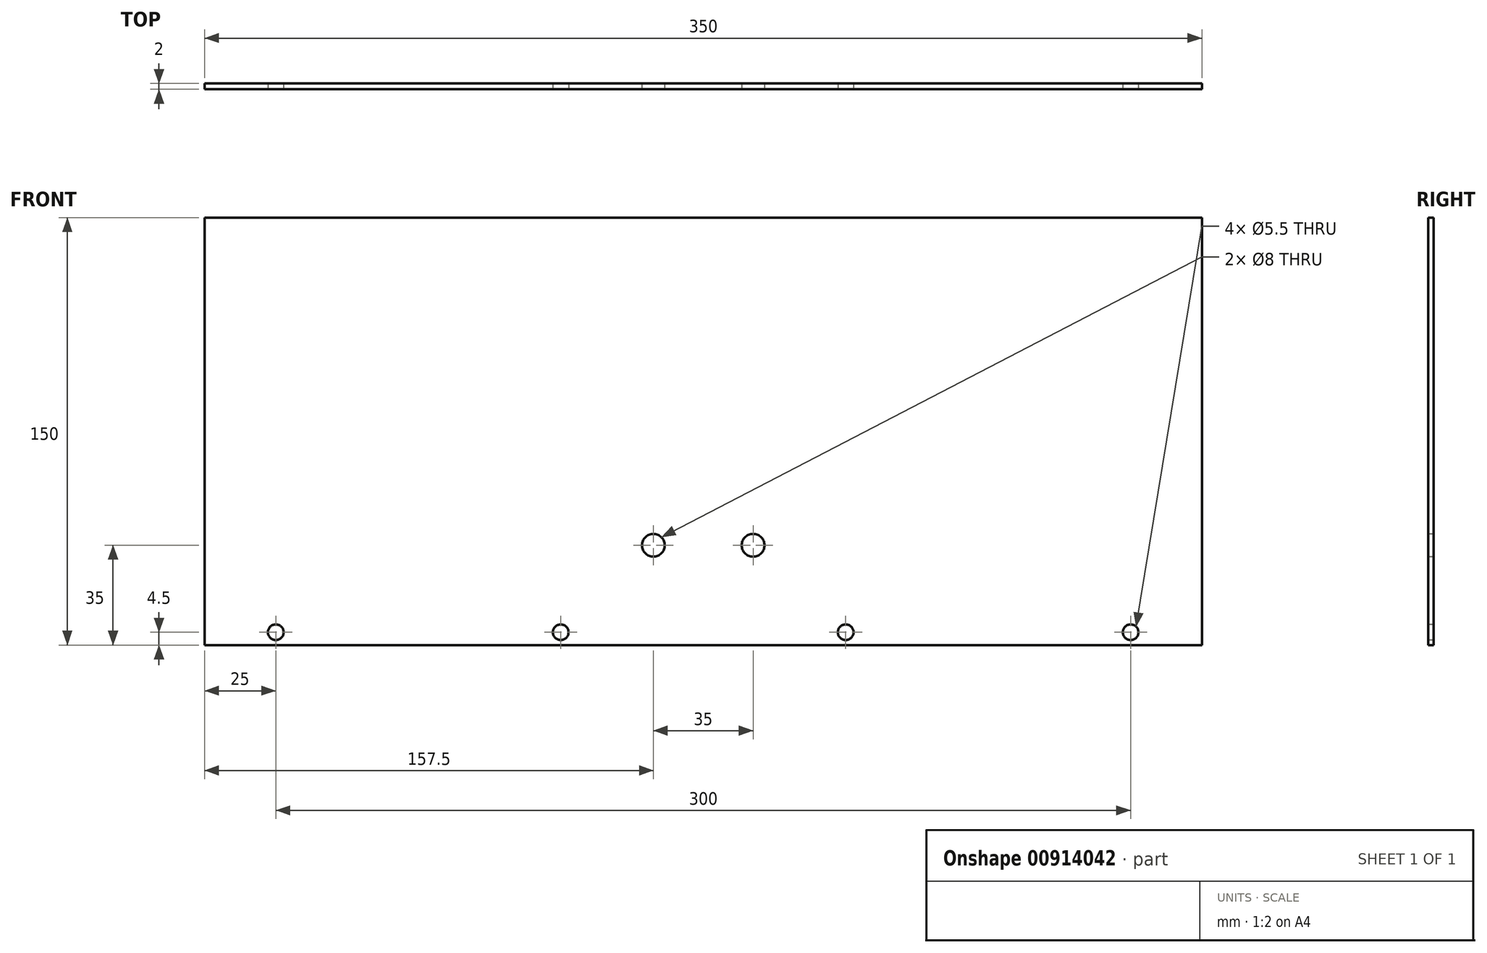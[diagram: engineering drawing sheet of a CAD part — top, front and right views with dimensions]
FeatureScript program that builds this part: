
annotation { "Feature Type Name" : "Feature", "Feature Type Description" : "" }
export const myFeature = defineFeature(function(context is Context, id is Id, definition is map)
    precondition{}
    {
        {
            var Q0;
            Q0=qCreatedBy(makeId("Front.planeOp"),FACE);
            var sketch = newSketch(context, id + "F0", { "sketchPlane" : qUnion([Q0])});
            skLineSegment(sketch, "E0.bottom", {"start": v(-175, 75) * mm, "end": v(175, 75) * mm});
            skLineSegment(sketch, "E0.top", {"start": v(-175, -75) * mm, "end": v(175, -75) * mm});
            skLineSegment(sketch, "E0.left", {"start": v(-175, 75) * mm, "end": v(-175, -75) * mm});
            skLineSegment(sketch, "E0.right", {"start": v(175, 75) * mm, "end": v(175, -75) * mm});
            skPoint(sketch, "E0.middle", {"position": v(0, 0) * mm});
            skSolve(sketch);
        }
        {
            var Q0;
            Q0=makeQuery(id+"F0.imprint","IMPRINT",FACE,{"disambiguationData":[TD([[makeQuery(id+"F0.imprint","IMPRINT",EDGE,{"derivedFrom":sQuery(id+"F0.wireOp",EDGE,"E0.bottom")}),-1.0]])]});
            extrude(context, id + "F1", {"entities" : qUnion([Q0]), "depth" : 2 * mm, "offsetDistance" : 25 * mm});
        }
        {
            var Q0;
            Q0=makeQuery(id+"F1.opExtrude","CAP_FACE",FACE,{"disambiguationData":[OSD([sQuery(id+"F0.wireOp",EDGE,"E0.bottom"),sQuery(id+"F0.wireOp",EDGE,"E0.top"),sQuery(id+"F0.wireOp",EDGE,"E0.left"),sQuery(id+"F0.wireOp",EDGE,"E0.right")])],"isStart":false});
            var sketch = newSketch(context, id + "F2", { "sketchPlane" : qUnion([Q0])});
            skCircle(sketch, "E1", {"center": v(-17.5, -40) * mm, "radius": 4 * mm});
            skCircle(sketch, "E2", {"center": v(17.5, -40) * mm, "radius": 4 * mm});
            skLineSegment(sketch, "E3", {"start": v(-17.5, -40) * mm, "end": v(17.5, -40) * mm, "construction": true});
            skLineSegment(sketch, "E4", {"start": v(0, -40) * mm, "end": v(0, -75) * mm, "construction": true});
            skSolve(sketch);
        }
        {
            var Q0;
            Q0=makeQuery(id+"F2.imprint","IMPRINT",FACE,{"disambiguationData":[TD([[makeQuery(id+"F2.imprint","IMPRINT",EDGE,{"derivedFrom":sQuery(id+"F2.wireOp",EDGE,"E1")}),1.0]])]});
            var Q1;
            Q1=makeQuery(id+"F2.imprint","IMPRINT",FACE,{"disambiguationData":[TD([[makeQuery(id+"F2.imprint","IMPRINT",EDGE,{"derivedFrom":sQuery(id+"F2.wireOp",EDGE,"E2")}),1.0]])]});
            extrude(context, id + "F3", {"entities" : qUnion([Q0, Q1]), "operationType" : NewBodyOperationType.REMOVE, "oppositeDirection" : true, "depth" : 25 * mm, "offsetDistance" : 25 * mm});
        }
        {
            var Q0;
            Q0=makeQuery(id+"F1.opExtrude","CAP_FACE",FACE,{"disambiguationData":[OSD([sQuery(id+"F0.wireOp",EDGE,"E0.bottom"),sQuery(id+"F0.wireOp",EDGE,"E0.top"),sQuery(id+"F0.wireOp",EDGE,"E0.left"),sQuery(id+"F0.wireOp",EDGE,"E0.right")])],"isStart":false});
            var sketch = newSketch(context, id + "F4", { "sketchPlane" : qUnion([Q0])});
            skLineSegment(sketch, "E5", {"start": v(-175, -70.5) * mm, "end": v(-150, -70.5) * mm});
            skLineSegment(sketch, "E6", {"start": v(-150, -70.5) * mm, "end": v(-50, -70.5) * mm});
            skLineSegment(sketch, "E7", {"start": v(-50, -70.5) * mm, "end": v(50, -70.5) * mm});
            skLineSegment(sketch, "E8", {"start": v(50, -70.5) * mm, "end": v(150, -70.5) * mm});
            skSolve(sketch);
        }
        {
            var Q0;
            Q0=sQuery(id+"F4.wireOp",VERTEX,"E5.end");
            var Q1;
            Q1=sQuery(id+"F4.wireOp",VERTEX,"E6.end");
            var Q2;
            Q2=sQuery(id+"F4.wireOp",VERTEX,"E7.end");
            var Q3;
            Q3=sQuery(id+"F4.wireOp",VERTEX,"E8.end");
            var Q4;
            Q4=makeQuery(id+"F1.opExtrude","SWEPT_BODY",BODY,{"disambiguationData":[OSD([sQuery(id+"F0.wireOp",EDGE,"E0.bottom"),sQuery(id+"F0.wireOp",EDGE,"E0.top"),sQuery(id+"F0.wireOp",EDGE,"E0.left"),sQuery(id+"F0.wireOp",EDGE,"E0.right")])]});
            hole(context, id + "F5", {"style" : HoleStyle.SIMPLE, "endStyle" : HoleEndStyle.BLIND, "standardTappedOrClearance" : lookupTablePath({ "fit" : "Normal", "standard" : "ISO", "size" : "M5", "type" : "Clearance" }), "standardBlindInLast" : lookupTablePath({ "fit" : "Normal", "standard" : "ISO", "size" : "M5", "type" : "Clearance" }), "holeDiameter" : 5.5 * mm, "majorDiameter" : 6 * mm, "holeDepth" : 13 * mm, "isTappedThrough" : true, "tappedDepth" : 10 * mm, "tapClearance" : 3, "startFromSketch" : true, "locations" : qUnion([Q0, Q1, Q2, Q3]), "scope" : qUnion([Q4])});
        }
    });
